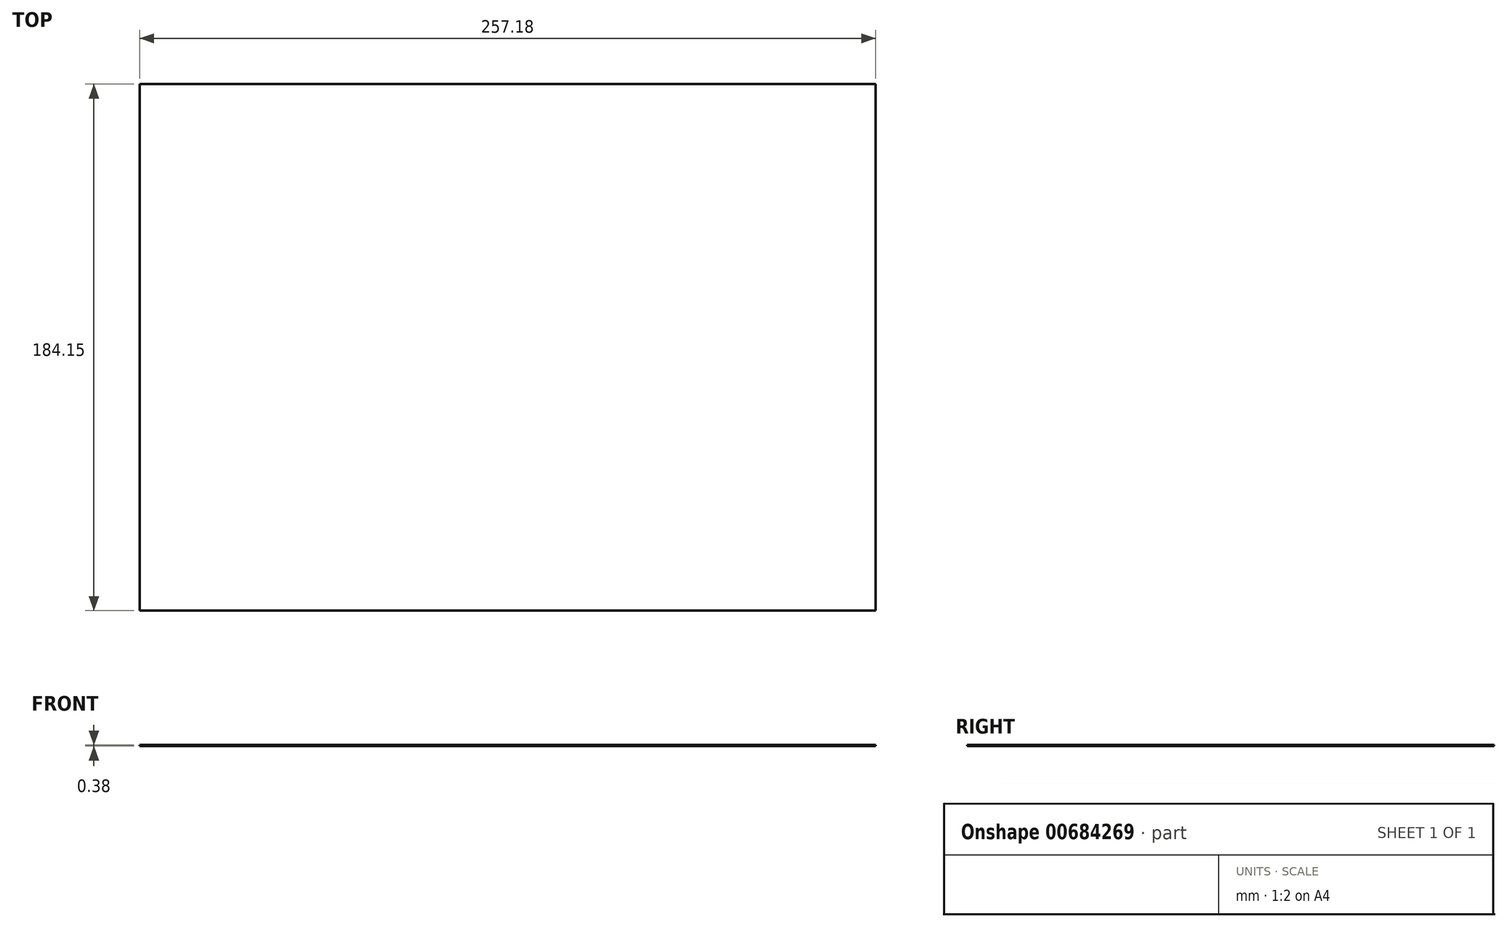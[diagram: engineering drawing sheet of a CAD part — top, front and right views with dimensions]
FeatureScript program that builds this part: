
annotation { "Feature Type Name" : "Feature", "Feature Type Description" : "" }
export const myFeature = defineFeature(function(context is Context, id is Id, definition is map)
    precondition{}
    {
        {
            var Q0;
            Q0=qCreatedBy(makeId("Top.planeOp"),FACE);
            var sketch = newSketch(context, id + "F0", { "sketchPlane" : qUnion([Q0])});
            skLineSegment(sketch, "E0.bottom", {"start": v(-128.59, 0) * mm, "end": v(128.59, 0) * mm});
            skLineSegment(sketch, "E0.top", {"start": v(-128.59, 184.15) * mm, "end": v(128.59, 184.15) * mm});
            skLineSegment(sketch, "E0.left", {"start": v(-128.59, 0) * mm, "end": v(-128.59, 184.15) * mm});
            skLineSegment(sketch, "E0.right", {"start": v(128.59, 0) * mm, "end": v(128.59, 184.15) * mm});
            skSolve(sketch);
        }
        {
            var Q0;
            Q0=makeQuery(id+"F0.imprint","IMPRINT",FACE,{"disambiguationData":[TD([[makeQuery(id+"F0.imprint","IMPRINT",EDGE,{"derivedFrom":sQuery(id+"F0.wireOp",EDGE,"E0.bottom")}),1.0]])]});
            extrude(context, id + "F1", {"entities" : qUnion([Q0]), "oppositeDirection" : true, "depth" : 0.38 * mm, "offsetDistance" : 25.4 * mm});
        }
    });
